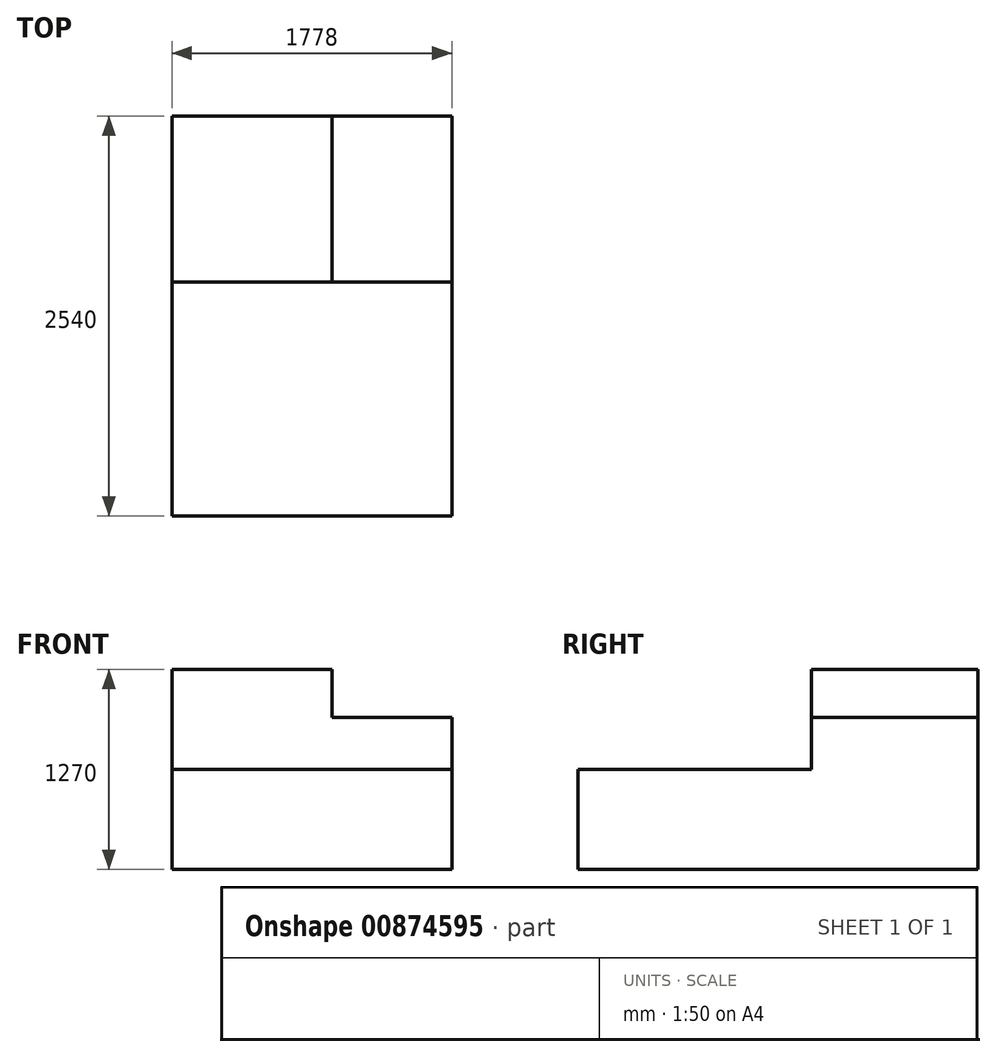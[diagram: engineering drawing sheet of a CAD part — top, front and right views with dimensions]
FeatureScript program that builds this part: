
annotation { "Feature Type Name" : "Feature", "Feature Type Description" : "" }
export const myFeature = defineFeature(function(context is Context, id is Id, definition is map)
    precondition{}
    {
        {
            var Q0;
            Q0=qCreatedBy(makeId("Top.planeOp"),FACE);
            var sketch = newSketch(context, id + "F0", { "sketchPlane" : qUnion([Q0])});
            skLineSegment(sketch, "E0.bottom", {"start": v(0, 0) * mm, "end": v(-1778, 0) * mm});
            skLineSegment(sketch, "E0.top", {"start": v(0, -2540) * mm, "end": v(-1778, -2540) * mm});
            skLineSegment(sketch, "E0.left", {"start": v(0, 0) * mm, "end": v(0, -2540) * mm});
            skLineSegment(sketch, "E0.right", {"start": v(-1778, 0) * mm, "end": v(-1778, -2540) * mm});
            skSolve(sketch);
        }
        {
            var Q0;
            Q0 = qSketchRegion(id + "F0", true);
            extrude(context, id + "F1", {"entities" : qUnion([Q0]), "depth" : 635 * mm, "offsetDistance" : 25.4 * mm});
        }
        {
            var Q0;
            Q0=makeQuery(id+"F1.opExtrude","CAP_FACE",FACE,{"disambiguationData":[OSD([sQuery(id+"F0.wireOp",EDGE,"E0.bottom"),sQuery(id+"F0.wireOp",EDGE,"E0.top"),sQuery(id+"F0.wireOp",EDGE,"E0.left"),sQuery(id+"F0.wireOp",EDGE,"E0.right")])],"isStart":false});
            var sketch = newSketch(context, id + "F2", { "sketchPlane" : qUnion([Q0])});
            skLineSegment(sketch, "E1.bottom", {"start": v(-1778, 0) * mm, "end": v(0, 0) * mm});
            skLineSegment(sketch, "E1.top", {"start": v(-1778, -1055.63) * mm, "end": v(0, -1055.63) * mm});
            skLineSegment(sketch, "E1.left", {"start": v(-1778, 0) * mm, "end": v(-1778, -1055.63) * mm});
            skLineSegment(sketch, "E1.right", {"start": v(0, 0) * mm, "end": v(0, -1055.63) * mm});
            skLineSegment(sketch, "E2.bottom", {"start": v(-1778, 0) * mm, "end": v(-762, 0) * mm});
            skLineSegment(sketch, "E2.top", {"start": v(-1778, -1055.63) * mm, "end": v(-762, -1055.63) * mm});
            skLineSegment(sketch, "E2.right", {"start": v(-762, 0) * mm, "end": v(-762, -1055.63) * mm});
            skSolve(sketch);
        }
        {
            var Q0;
            Q0=makeQuery(id+"F2.imprint","IMPRINT",FACE,{"disambiguationData":[TD([[makeQuery(id+"F2.imprint","IMPRINT",EDGE,{"derivedFrom":sQuery(id+"F2.wireOp",EDGE,"E1.bottom")}),1.0]])]});
            extrude(context, id + "F3", {"entities" : qUnion([Q0]), "operationType" : NewBodyOperationType.ADD, "depth" : 330.2 * mm, "offsetDistance" : 25.4 * mm});
        }
        {
            var Q0;
            Q0=makeQuery(id+"F1.opExtrude","CAP_FACE",FACE,{"disambiguationData":[OSD([sQuery(id+"F0.wireOp",EDGE,"E0.bottom"),sQuery(id+"F0.wireOp",EDGE,"E0.top"),sQuery(id+"F0.wireOp",EDGE,"E0.left"),sQuery(id+"F0.wireOp",EDGE,"E0.right")])],"isStart":false});
            var sketch = newSketch(context, id + "F4", { "sketchPlane" : qUnion([Q0])});
            skLineSegment(sketch, "E3.bottom", {"start": v(-762, -1055.63) * mm, "end": v(-1778, -1055.63) * mm});
            skLineSegment(sketch, "E3.top", {"start": v(-762, 0) * mm, "end": v(-1778, 0) * mm});
            skLineSegment(sketch, "E3.left", {"start": v(-762, -1055.63) * mm, "end": v(-762, 0) * mm});
            skLineSegment(sketch, "E3.right", {"start": v(-1778, -1055.63) * mm, "end": v(-1778, 0) * mm});
            skSolve(sketch);
        }
        {
            var Q0;
            Q0 = qSketchRegion(id + "F4", true);
            extrude(context, id + "F5", {"entities" : qUnion([Q0]), "operationType" : NewBodyOperationType.ADD, "depth" : 635 * mm, "offsetDistance" : 25.4 * mm});
        }
    });
